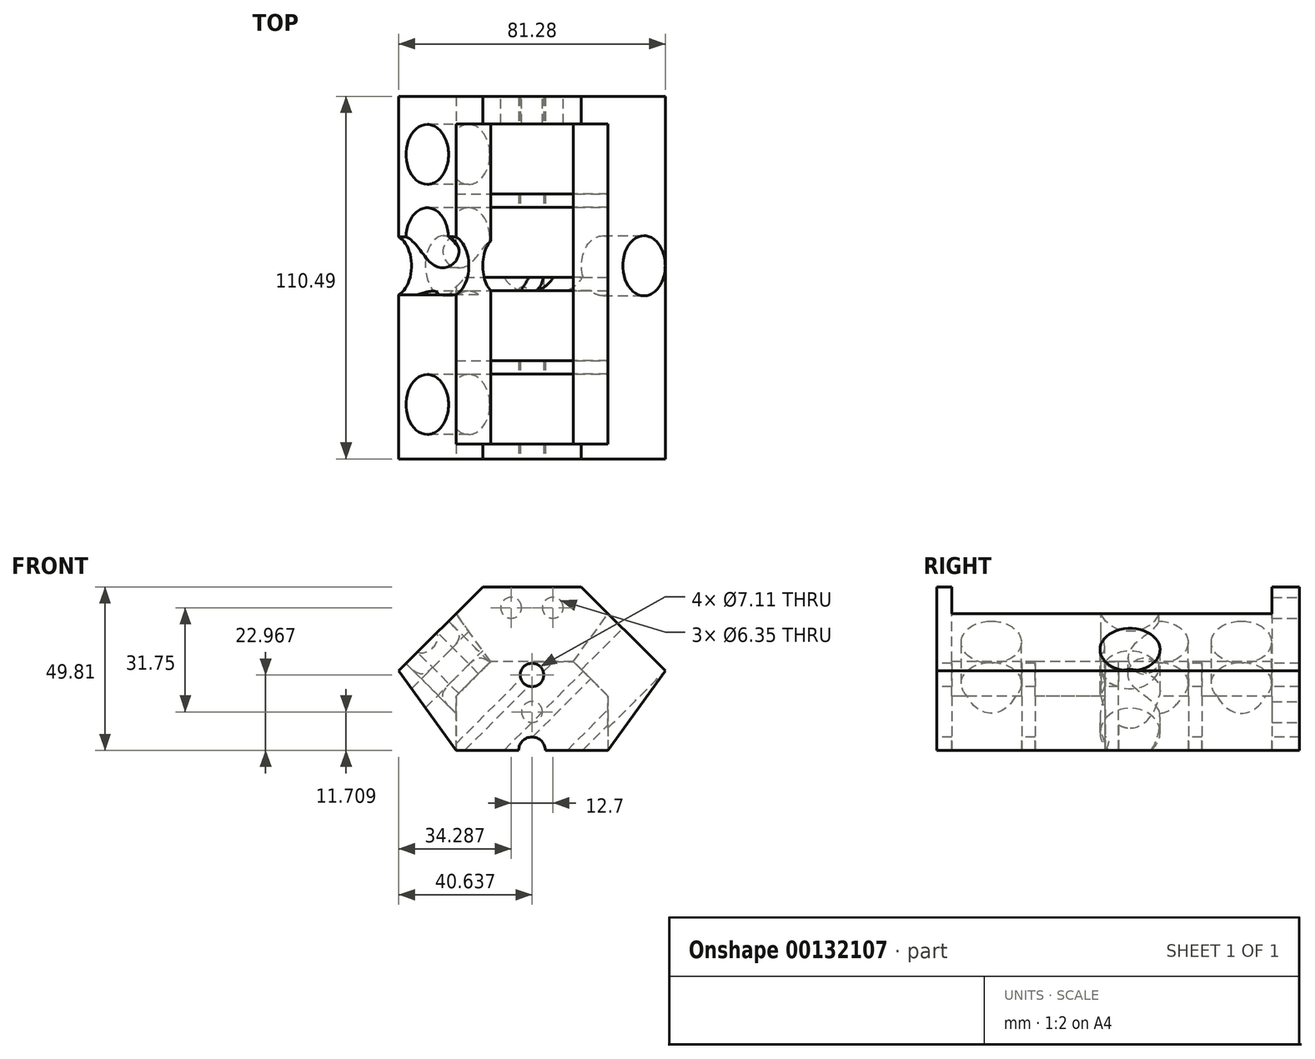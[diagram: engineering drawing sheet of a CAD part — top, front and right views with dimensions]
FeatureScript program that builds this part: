
annotation { "Feature Type Name" : "Feature", "Feature Type Description" : "" }
export const myFeature = defineFeature(function(context is Context, id is Id, definition is map)
    precondition{}
    {
        {
            var Q0;
            Q0=qCreatedBy(makeId("Top.planeOp"),FACE);
            var sketch = newSketch(context, id + "F0", { "sketchPlane" : qUnion([Q0])});
            skLineSegment(sketch, "E0.bottom", {"start": v(-50.32, 362.69) * mm, "end": v(356.08, 362.69) * mm});
            skLineSegment(sketch, "E0.top", {"start": v(-50.32, -189.76) * mm, "end": v(356.08, -189.76) * mm});
            skLineSegment(sketch, "E0.left", {"start": v(-50.32, 362.69) * mm, "end": v(-50.32, -189.76) * mm});
            skLineSegment(sketch, "E0.right", {"start": v(356.08, 362.69) * mm, "end": v(356.08, -189.76) * mm});
            skPoint(sketch, "E1.right.end.orphan", {"position": v(268.7, 221.15) * mm});
            skPoint(sketch, "E2.end.orphan", {"position": v(268.7, 119.55) * mm});
            skPoint(sketch, "E3.right.end.orphan", {"position": v(268.7, 66.78) * mm});
            skPoint(sketch, "E4.end.orphan", {"position": v(268.7, -34.82) * mm});
            skPoint(sketch, "E5.top.end.orphan", {"position": v(268.7, -62.76) * mm});
            skLineSegment(sketch, "E6.bottom", {"start": v(37.06, -166.9) * mm, "end": v(268.7, -166.9) * mm});
            skLineSegment(sketch, "E6.top", {"start": v(37.06, -60.22) * mm, "end": v(268.7, -60.22) * mm});
            skLineSegment(sketch, "E6.left", {"start": v(37.06, -166.9) * mm, "end": v(37.06, -60.22) * mm});
            skLineSegment(sketch, "E6.right", {"start": v(268.7, -166.9) * mm, "end": v(268.7, -60.22) * mm});
            skPoint(sketch, "E7.endSnap0", {"position": v(152.88, -189.76) * mm});
            skLineSegment(sketch, "E8.bottom", {"start": v(37.06, 320.78) * mm, "end": v(268.7, 320.78) * mm});
            skLineSegment(sketch, "E8.top", {"start": v(37.06, 214.1) * mm, "end": v(268.7, 214.1) * mm});
            skLineSegment(sketch, "E8.left", {"start": v(37.06, 320.78) * mm, "end": v(37.06, 214.1) * mm});
            skLineSegment(sketch, "E8.right", {"start": v(268.7, 320.78) * mm, "end": v(268.7, 214.1) * mm});
            skLineSegment(sketch, "E9.bottom", {"start": v(37.06, 193.78) * mm, "end": v(268.7, 193.78) * mm});
            skLineSegment(sketch, "E9.top", {"start": v(37.06, 87.1) * mm, "end": v(268.7, 87.1) * mm});
            skLineSegment(sketch, "E9.left", {"start": v(37.06, 193.78) * mm, "end": v(37.06, 87.1) * mm});
            skLineSegment(sketch, "E9.right", {"start": v(268.7, 193.78) * mm, "end": v(268.7, 87.1) * mm});
            skLineSegment(sketch, "E10.right", {"start": v(268.7, -34.82) * mm, "end": v(268.7, -39.9) * mm});
            skLineSegment(sketch, "E11.bottom", {"start": v(37.06, 66.78) * mm, "end": v(268.7, 66.78) * mm});
            skLineSegment(sketch, "E11.top", {"start": v(37.06, -39.9) * mm, "end": v(268.7, -39.9) * mm});
            skLineSegment(sketch, "E11.left", {"start": v(37.06, 66.78) * mm, "end": v(37.06, -39.9) * mm});
            skLineSegment(sketch, "E11.right", {"start": v(268.7, 66.78) * mm, "end": v(268.7, -39.9) * mm});
            skPoint(sketch, "E7.end.orphan", {"position": v(268.7, -189.76) * mm});
            skPoint(sketch, "E12.start.orphan", {"position": v(268.7, 320.78) * mm});
            skSolve(sketch);
        }
        {
            var Q0;
            Q0=makeQuery(id+"F0.imprint","IMPRINT",FACE,{"disambiguationData":[TD([[makeQuery(id+"F0.imprint","IMPRINT",EDGE,{"derivedFrom":sQuery(id+"F0.wireOp",EDGE,"E0.bottom")}),-1.0]])]});
            extrude(context, id + "F1", {"entities" : qUnion([Q0]), "depth" : 249.05 * mm});
        }
        {
            var Q0;
            Q0=makeQuery(id+"F1.opExtrude","SWEPT_FACE",FACE,{"disambiguationData":[OSD([sQuery(id+"F0.wireOp",EDGE,"E0.top")])]});
            var sketch = newSketch(context, id + "F2", { "sketchPlane" : qUnion([Q0])});
            skLineSegment(sketch, "E13", {"start": v(152.88, 0) * mm, "end": v(37.06, 0) * mm, "construction": true});
            skLineSegment(sketch, "E14", {"start": v(152.88, 0) * mm, "end": v(268.7, 0) * mm, "construction": true});
            skLineSegment(sketch, "E15", {"start": v(152.88, 0) * mm, "end": v(152.88, -265.94) * mm, "construction": true});
            skLineSegment(sketch, "E16", {"start": v(152.88, 0) * mm, "end": v(-102.56, -255.45) * mm, "construction": true});
            skLineSegment(sketch, "E17", {"start": v(-22.58, -175.46) * mm, "end": v(-184.67, -13.37) * mm, "construction": true});
            skLineSegment(sketch, "E18", {"start": v(-184.67, -13.37) * mm, "end": v(-50.32, 120.99) * mm, "construction": true});
            skLineSegment(sketch, "E19", {"start": v(37.06, 0) * mm, "end": v(-50.32, 120.99) * mm});
            skLineSegment(sketch, "E20", {"start": v(-50.32, 0) * mm, "end": v(37.06, 0) * mm});
            skLineSegment(sketch, "E21", {"start": v(-50.32, 120.99) * mm, "end": v(-50.32, 0) * mm});
            skLineSegment(sketch, "E22", {"start": v(152.88, 0) * mm, "end": v(426.24, -273.36) * mm, "construction": true});
            skLineSegment(sketch, "E23", {"start": v(328.35, -175.46) * mm, "end": v(490.44, -13.37) * mm, "construction": true});
            skLineSegment(sketch, "E24", {"start": v(490.44, -13.37) * mm, "end": v(356.08, 120.99) * mm, "construction": true});
            skLineSegment(sketch, "E25", {"start": v(268.7, 0) * mm, "end": v(356.08, 120.99) * mm});
            skLineSegment(sketch, "E26", {"start": v(356.08, 120.99) * mm, "end": v(356.08, 0) * mm});
            skLineSegment(sketch, "E27", {"start": v(268.7, 0) * mm, "end": v(356.08, 0) * mm});
            skLineSegment(sketch, "E28", {"start": v(-184.67, -13.37) * mm, "end": v(77.74, 249.05) * mm, "construction": true});
            skLineSegment(sketch, "E29", {"start": v(490.44, -13.37) * mm, "end": v(228.02, 249.05) * mm, "construction": true});
            skLineSegment(sketch, "E30", {"start": v(77.74, 249.05) * mm, "end": v(-50.32, 249.05) * mm});
            skLineSegment(sketch, "E31", {"start": v(-50.32, 249.05) * mm, "end": v(-50.32, 120.99) * mm});
            skLineSegment(sketch, "E32", {"start": v(-50.32, 120.99) * mm, "end": v(77.74, 249.05) * mm});
            skLineSegment(sketch, "E33", {"start": v(228.02, 249.05) * mm, "end": v(356.08, 249.05) * mm});
            skLineSegment(sketch, "E34", {"start": v(356.08, 249.05) * mm, "end": v(356.08, 120.99) * mm});
            skLineSegment(sketch, "E35", {"start": v(356.08, 120.99) * mm, "end": v(228.02, 249.05) * mm});
            skLineSegment(sketch, "E36", {"start": v(152.88, 249.05) * mm, "end": v(152.88, 344.64) * mm, "construction": true});
            skLineSegment(sketch, "E37", {"start": v(152.88, 344.64) * mm, "end": v(46.2, 344.64) * mm, "construction": true});
            skLineSegment(sketch, "E38", {"start": v(152.88, 344.64) * mm, "end": v(259.56, 344.64) * mm, "construction": true});
            skLineSegment(sketch, "E39", {"start": v(259.56, 344.64) * mm, "end": v(259.56, 217.5) * mm, "construction": true});
            skLineSegment(sketch, "E40", {"start": v(46.2, 344.64) * mm, "end": v(46.2, 217.5) * mm, "construction": true});
            skCircle(sketch, "E41", {"center": v(152.88, 0) * mm, "radius": 20.32 * mm});
            skLineSegment(sketch, "E42", {"start": v(152.88, 0) * mm, "end": v(152.88, 114.83) * mm, "construction": true});
            skCircle(sketch, "E43", {"center": v(152.88, 114.83) * mm, "radius": 17.78 * mm});
            skLineSegment(sketch, "E44", {"start": v(152.88, 114.83) * mm, "end": v(152.88, 132.61) * mm, "construction": true});
            skLineSegment(sketch, "E45", {"start": v(152.88, 132.61) * mm, "end": v(152.88, 249.05) * mm, "construction": true});
            skLineSegment(sketch, "E46", {"start": v(152.88, 249.05) * mm, "end": v(152.88, 147.45) * mm});
            skSolve(sketch);
        }
        {
            var Q0;
            Q0=makeQuery(id+"F2.imprint","IMPRINT",FACE,{"disambiguationData":[TD([[makeQuery(id+"F2.imprint","IMPRINT",EDGE,{"derivedFrom":sQuery(id+"F2.wireOp",EDGE,"E19")}),1.0]])]});
            extrude(context, id + "F3", {"entities" : qUnion([Q0]), "operationType" : NewBodyOperationType.REMOVE, "oppositeDirection" : true, "depth" : 1497.04 * mm});
        }
        {
            var Q0;
            Q0=makeQuery(id+"F2.imprint","IMPRINT",FACE,{"disambiguationData":[TD([[makeQuery(id+"F2.imprint","IMPRINT",EDGE,{"derivedFrom":sQuery(id+"F2.wireOp",EDGE,"E25")}),-1.0]])]});
            extrude(context, id + "F4", {"entities" : qUnion([Q0]), "operationType" : NewBodyOperationType.REMOVE, "oppositeDirection" : true, "depth" : 679.38 * mm});
        }
        {
            var Q0;
            Q0=makeQuery(id+"F2.imprint","IMPRINT",FACE,{"disambiguationData":[TD([[makeQuery(id+"F2.imprint","IMPRINT",EDGE,{"derivedFrom":sQuery(id+"F2.wireOp",EDGE,"E30")}),-1.0]])]});
            extrude(context, id + "F5", {"entities" : qUnion([Q0]), "operationType" : NewBodyOperationType.REMOVE, "oppositeDirection" : true, "depth" : 711.26 * mm});
        }
        {
            var Q0;
            Q0=makeQuery(id+"F2.imprint","IMPRINT",FACE,{"disambiguationData":[TD([[makeQuery(id+"F2.imprint","IMPRINT",EDGE,{"derivedFrom":sQuery(id+"F2.wireOp",EDGE,"E33")}),-1.0]])]});
            extrude(context, id + "F6", {"entities" : qUnion([Q0]), "operationType" : NewBodyOperationType.REMOVE, "oppositeDirection" : true, "depth" : 1229.88 * mm});
        }
        {
            var Q0;
            {var subQ0=sQuery(id+"F2.wireOp",EDGE,"E41");var subQ1=makeQuery(id+"F1.opExtrude","CAP_EDGE",EDGE,{"disambiguationData":[OSD([sQuery(id+"F0.wireOp",EDGE,"E0.top")])],"isStart":true});var subQ2=makeQuery(id+"F2.imprint","INTERSECT",VERTEX,{"disambiguationData":[OD(0.0)],"derivedFrom":[subQ1,subQ0]});Q0=makeQuery(id+"F2.imprint","IMPRINT",FACE,{"disambiguationData":[TD([[makeQuery(id+"F2.imprint","IMPRINT",EDGE,{"disambiguationData":[TD([[subQ2,1.0]])],"derivedFrom":subQ0}),1.0]])]});}
            extrude(context, id + "F7", {"entities" : qUnion([Q0]), "operationType" : NewBodyOperationType.REMOVE, "oppositeDirection" : true, "depth" : 578.05 * mm});
        }
        {
            var Q0;
            Q0=makeQuery(id+"F2.imprint","IMPRINT",FACE,{"disambiguationData":[TD([[makeQuery(id+"F2.imprint","IMPRINT",EDGE,{"derivedFrom":sQuery(id+"F2.wireOp",EDGE,"E43")}),1.0]])]});
            extrude(context, id + "F8", {"entities" : qUnion([Q0]), "operationType" : NewBodyOperationType.REMOVE, "oppositeDirection" : true, "depth" : 729.74 * mm});
        }
        {
            var Q0;
            Q0=makeQuery(id+"F1.opExtrude","SWEPT_FACE",FACE,{"disambiguationData":[OSD([sQuery(id+"F0.wireOp",EDGE,"E6.top")])]});
            var sketch = newSketch(context, id + "F9", { "sketchPlane" : qUnion([Q0])});
            skPoint(sketch, "E47.endSnap0", {"position": v(152.88, 249.05) * mm});
            skLineSegment(sketch, "E48", {"start": v(152.88, 135.38) * mm, "end": v(37.06, 135.38) * mm});
            skLineSegment(sketch, "E49", {"start": v(37.06, 135.38) * mm, "end": v(268.7, 135.38) * mm});
            skLineSegment(sketch, "E50", {"start": v(268.7, 135.38) * mm, "end": v(268.7, 208.36) * mm});
            skLineSegment(sketch, "E51", {"start": v(268.7, 208.36) * mm, "end": v(228.02, 249.05) * mm});
            skLineSegment(sketch, "E52", {"start": v(228.02, 249.05) * mm, "end": v(77.74, 249.05) * mm});
            skLineSegment(sketch, "E53", {"start": v(77.74, 249.05) * mm, "end": v(37.06, 208.36) * mm});
            skLineSegment(sketch, "E54", {"start": v(37.06, 135.38) * mm, "end": v(37.06, 208.36) * mm});
            skLineSegment(sketch, "E55", {"start": v(37.06, 208.36) * mm, "end": v(89.77, 135.38) * mm});
            skLineSegment(sketch, "E56", {"start": v(268.7, 208.36) * mm, "end": v(216, 135.38) * mm});
            skSolve(sketch);
        }
        {
            var Q0;
            Q0=makeQuery(id+"F9.imprint","IMPRINT",FACE,{"disambiguationData":[TD([[makeQuery(id+"F9.imprint","IMPRINT",EDGE,{"derivedFrom":sQuery(id+"F9.wireOp",EDGE,"E51")}),-1.0]])]});
            extrude(context, id + "F10", {"entities" : qUnion([Q0]), "operationType" : NewBodyOperationType.REMOVE, "oppositeDirection" : true, "depth" : 324.26 * mm});
        }
        {
            var Q0;
            Q0=makeQuery(id+"F1.opExtrude","SWEPT_FACE",FACE,{"disambiguationData":[OSD([sQuery(id+"F0.wireOp",EDGE,"E11.top")])]});
            var sketch = newSketch(context, id + "F11", { "sketchPlane" : qUnion([Q0])});
            skLineSegment(sketch, "E57", {"start": v(-89.77, 135.38) * mm, "end": v(-37.06, 208.36) * mm});
            skLineSegment(sketch, "E58", {"start": v(-89.77, 135.38) * mm, "end": v(-37.06, 135.38) * mm});
            skLineSegment(sketch, "E59", {"start": v(-37.06, 135.38) * mm, "end": v(-37.06, 208.36) * mm});
            skSolve(sketch);
        }
        {
            var Q0;
            Q0=qSketchRegion(id+"F11",true);
            extrude(context, id + "F12", {"entities" : qUnion([Q0]), "operationType" : NewBodyOperationType.ADD, "depth" : 368.3 * mm, "hasSecondDirection" : true, "secondDirectionOppositeDirection" : true, "secondDirectionDepth" : 127 * mm});
        }
        {
            var Q0;
            Q0=makeQuery(id+"F1.opExtrude","SWEPT_FACE",FACE,{"disambiguationData":[OSD([sQuery(id+"F0.wireOp",EDGE,"E11.top")])]});
            var sketch = newSketch(context, id + "F13", { "sketchPlane" : qUnion([Q0])});
            skLineSegment(sketch, "E60", {"start": v(-216, 135.38) * mm, "end": v(-268.7, 135.38) * mm});
            skLineSegment(sketch, "E61", {"start": v(-268.7, 135.38) * mm, "end": v(-268.7, 208.36) * mm});
            skLineSegment(sketch, "E62", {"start": v(-268.7, 208.36) * mm, "end": v(-216, 135.38) * mm});
            skSolve(sketch);
        }
        {
            var Q0;
            Q0=qSketchRegion(id+"F13",true);
            extrude(context, id + "F14", {"entities" : qUnion([Q0]), "operationType" : NewBodyOperationType.ADD, "depth" : 368.3 * mm, "hasSecondDirection" : true, "secondDirectionOppositeDirection" : true, "secondDirectionDepth" : 127 * mm});
        }
        {
            var Q0;
            Q0=makeQuery(id+"F1.opExtrude","SWEPT_FACE",FACE,{"disambiguationData":[OSD([sQuery(id+"F0.wireOp",EDGE,"E9.top")])]});
            var sketch = newSketch(context, id + "F15", { "sketchPlane" : qUnion([Q0])});
            skLineSegment(sketch, "E63", {"start": v(-89.77, 135.38) * mm, "end": v(-37.06, 82.68) * mm});
            skLineSegment(sketch, "E64", {"start": v(-37.06, 82.68) * mm, "end": v(-37.06, 135.38) * mm});
            skLineSegment(sketch, "E65", {"start": v(-37.06, 135.38) * mm, "end": v(-89.77, 135.38) * mm});
            skLineSegment(sketch, "E66", {"start": v(-216, 135.38) * mm, "end": v(-268.7, 82.68) * mm});
            skLineSegment(sketch, "E67", {"start": v(-268.7, 82.68) * mm, "end": v(-268.7, 135.38) * mm});
            skLineSegment(sketch, "E68", {"start": v(-268.7, 135.38) * mm, "end": v(-216, 135.38) * mm});
            skSolve(sketch);
        }
        {
            var Q0;
            Q0=makeQuery(id+"F15.imprint","IMPRINT",FACE,{"disambiguationData":[TD([[makeQuery(id+"F15.imprint","IMPRINT",EDGE,{"derivedFrom":sQuery(id+"F15.wireOp",EDGE,"E63")}),1.0]])]});
            extrude(context, id + "F16", {"entities" : qUnion([Q0]), "operationType" : NewBodyOperationType.ADD, "depth" : 249.12 * mm, "hasSecondDirection" : true, "secondDirectionOppositeDirection" : true, "secondDirectionDepth" : 267.4 * mm});
        }
        {
            var Q0;
            Q0=makeQuery(id+"F15.imprint","IMPRINT",FACE,{"disambiguationData":[TD([[makeQuery(id+"F15.imprint","IMPRINT",EDGE,{"derivedFrom":sQuery(id+"F15.wireOp",EDGE,"E66")}),-1.0]])]});
            extrude(context, id + "F17", {"entities" : qUnion([Q0]), "operationType" : NewBodyOperationType.ADD, "depth" : 272.47 * mm, "hasSecondDirection" : true, "secondDirectionOppositeDirection" : true, "secondDirectionDepth" : 265.33 * mm});
        }
        {
            var Q0;
            Q0=makeQuery(id+"F6.boolean.opBoolean","COPY",FACE,{"derivedFrom":makeQuery(id+"F6.opExtrude","SWEPT_FACE",FACE,{"disambiguationData":[OSD([sQuery(id+"F2.wireOp",EDGE,"E35")])]})});
            var sketch = newSketch(context, id + "F18", { "sketchPlane" : qUnion([Q0])});
            skLineSegment(sketch, "E69", {"start": v(42.67, -166.9) * mm, "end": v(166.24, -166.9) * mm});
            skLineSegment(sketch, "E70", {"start": v(42.67, 320.78) * mm, "end": v(166.24, 320.78) * mm});
            skLineSegment(sketch, "E71", {"start": v(104.45, -166.9) * mm, "end": v(104.45, -60.22) * mm});
            skLineSegment(sketch, "E72", {"start": v(104.45, -39.9) * mm, "end": v(104.45, 66.78) * mm});
            skLineSegment(sketch, "E73", {"start": v(104.45, 87.1) * mm, "end": v(104.45, 193.78) * mm});
            skLineSegment(sketch, "E74", {"start": v(104.45, 214.1) * mm, "end": v(104.45, 320.78) * mm});
            skLineSegment(sketch, "E75", {"start": v(104.45, -113.56) * mm, "end": v(166.24, -113.56) * mm});
            skLineSegment(sketch, "E76", {"start": v(104.45, 13.44) * mm, "end": v(166.24, 13.44) * mm});
            skLineSegment(sketch, "E77", {"start": v(104.45, 140.44) * mm, "end": v(166.24, 140.44) * mm});
            skLineSegment(sketch, "E78", {"start": v(104.45, 267.44) * mm, "end": v(166.24, 267.44) * mm});
            skLineSegment(sketch, "E79", {"start": v(119.9, -120.23) * mm, "end": v(104.45, -120.23) * mm});
            skCircle(sketch, "E80", {"center": v(104.45, -120.23) * mm, "radius": 45.72 * mm});
            skLineSegment(sketch, "E81", {"start": v(135.35, 13.44) * mm, "end": v(135.35, 6.75) * mm});
            skLineSegment(sketch, "E82", {"start": v(135.35, 140.44) * mm, "end": v(135.35, 133.75) * mm});
            skLineSegment(sketch, "E83", {"start": v(135.35, 267.44) * mm, "end": v(135.35, 260.75) * mm});
            skLineSegment(sketch, "E84", {"start": v(135.35, 6.75) * mm, "end": v(104.45, 6.75) * mm});
            skLineSegment(sketch, "E85", {"start": v(135.35, 133.75) * mm, "end": v(104.45, 133.75) * mm});
            skLineSegment(sketch, "E86", {"start": v(135.35, 260.75) * mm, "end": v(104.45, 260.75) * mm});
            skCircle(sketch, "E87", {"center": v(104.45, 6.75) * mm, "radius": 45.72 * mm});
            skCircle(sketch, "E88", {"center": v(104.45, 133.75) * mm, "radius": 45.72 * mm});
            skCircle(sketch, "E89", {"center": v(104.45, 260.75) * mm, "radius": 45.72 * mm});
            skSolve(sketch);
        }
        {
            var Q0;
            Q0 = qSketchRegion(id + "F18", true);
            var Q1;
            {var subQ4=sQuery(id+"F18.wireOp",EDGE,"E81");Q1=makeQuery(id+"F18.imprint","IMPRINT",FACE,{"disambiguationData":[TD([[makeQuery(id+"F18.imprint","IMPRINT",EDGE,{"derivedFrom":subQ4}),-1.0]])]});}
            var Q2;
            {var subQ4=sQuery(id+"F18.wireOp",EDGE,"E82");Q2=makeQuery(id+"F18.imprint","IMPRINT",FACE,{"disambiguationData":[TD([[makeQuery(id+"F18.imprint","IMPRINT",EDGE,{"derivedFrom":subQ4}),-1.0]])]});}
            var Q3;
            {var subQ4=sQuery(id+"F18.wireOp",EDGE,"E83");Q3=makeQuery(id+"F18.imprint","IMPRINT",FACE,{"disambiguationData":[TD([[makeQuery(id+"F18.imprint","IMPRINT",EDGE,{"derivedFrom":subQ4}),-1.0]])]});}
            extrude(context, id + "F19", {"entities" : qUnion([Q0, Q1, Q2, Q3]), "operationType" : NewBodyOperationType.REMOVE, "oppositeDirection" : true, "depth" : 558.8 * mm});
        }
        {
            var Q0;
            Q0=makeQuery(id+"F5.boolean.opBoolean","COPY",FACE,{"derivedFrom":makeQuery(id+"F5.opExtrude","SWEPT_FACE",FACE,{"disambiguationData":[OSD([sQuery(id+"F2.wireOp",EDGE,"E32")])]})});
            var sketch = newSketch(context, id + "F20", { "sketchPlane" : qUnion([Q0])});
            skLineSegment(sketch, "E90", {"start": v(-320.78, 173.54) * mm, "end": v(-320.78, 49.97) * mm});
            skLineSegment(sketch, "E91", {"start": v(-320.78, 111.76) * mm, "end": v(-319.84, 111.76) * mm});
            skLineSegment(sketch, "E92", {"start": v(-193.78, 111.76) * mm, "end": v(-192.84, 111.76) * mm});
            skLineSegment(sketch, "E93", {"start": v(-66.78, 111.76) * mm, "end": v(-65.84, 111.76) * mm});
            skLineSegment(sketch, "E94", {"start": v(60.22, 111.76) * mm, "end": v(61.16, 111.76) * mm});
            skCircle(sketch, "E95", {"center": v(-274.12, 111.76) * mm, "radius": 45.72 * mm});
            skCircle(sketch, "E96", {"center": v(-147.12, 111.76) * mm, "radius": 45.72 * mm});
            skCircle(sketch, "E97", {"center": v(-20.12, 111.76) * mm, "radius": 45.72 * mm});
            skCircle(sketch, "E98", {"center": v(106.88, 111.76) * mm, "radius": 45.72 * mm});
            skPoint(sketch, "E99.start.orphan", {"position": v(-267.44, 111.76) * mm});
            skLineSegment(sketch, "E100.trimOffspring", {"start": v(-228.4, 111.76) * mm, "end": v(-214.1, 111.76) * mm});
            skLineSegment(sketch, "E101.trimOffspring", {"start": v(-101.4, 111.76) * mm, "end": v(-87.1, 111.76) * mm});
            skPoint(sketch, "E102.orphan", {"position": v(-140.44, 111.76) * mm});
            skPoint(sketch, "E103.start.orphan", {"position": v(-13.44, 111.76) * mm});
            skLineSegment(sketch, "E104.trimOffspring", {"start": v(25.6, 111.76) * mm, "end": v(39.9, 111.76) * mm});
            skPoint(sketch, "E105.start.orphan", {"position": v(113.56, 111.76) * mm});
            skLineSegment(sketch, "E106.trimOffspring", {"start": v(152.6, 111.76) * mm, "end": v(166.9, 111.76) * mm});
            skSolve(sketch);
        }
        {
            var Q0;
            {var subQ0=sQuery(id+"F20.wireOp",EDGE,"E95");var subQ1=makeQuery(id+"F20.imprint","IMPRINT",VERTEX,{"disambiguationData":[OD(0.0)],"derivedFrom":subQ0});Q0=makeQuery(id+"F20.imprint","IMPRINT",FACE,{"disambiguationData":[TD([[makeQuery(id+"F20.imprint","IMPRINT",EDGE,{"disambiguationData":[TD([[subQ1,1.0]])],"derivedFrom":subQ0}),1.0]])]});}
            var Q1;
            {var subQ0=sQuery(id+"F20.wireOp",EDGE,"E96");var subQ1=makeQuery(id+"F20.imprint","IMPRINT",VERTEX,{"disambiguationData":[OD(0.0)],"derivedFrom":subQ0});Q1=makeQuery(id+"F20.imprint","IMPRINT",FACE,{"disambiguationData":[TD([[makeQuery(id+"F20.imprint","IMPRINT",EDGE,{"disambiguationData":[TD([[subQ1,1.0]])],"derivedFrom":subQ0}),1.0]])]});}
            var Q2;
            {var subQ0=sQuery(id+"F20.wireOp",EDGE,"E97");var subQ1=makeQuery(id+"F20.imprint","IMPRINT",VERTEX,{"disambiguationData":[OD(0.0)],"derivedFrom":subQ0});Q2=makeQuery(id+"F20.imprint","IMPRINT",FACE,{"disambiguationData":[TD([[makeQuery(id+"F20.imprint","IMPRINT",EDGE,{"disambiguationData":[TD([[subQ1,1.0]])],"derivedFrom":subQ0}),1.0]])]});}
            var Q3;
            {var subQ0=sQuery(id+"F20.wireOp",EDGE,"E98");var subQ1=makeQuery(id+"F20.imprint","IMPRINT",VERTEX,{"disambiguationData":[OD(0.0)],"derivedFrom":subQ0});Q3=makeQuery(id+"F20.imprint","IMPRINT",FACE,{"disambiguationData":[TD([[makeQuery(id+"F20.imprint","IMPRINT",EDGE,{"disambiguationData":[TD([[subQ1,1.0]])],"derivedFrom":subQ0}),1.0]])]});}
            extrude(context, id + "F21", {"entities" : qUnion([Q0, Q1, Q2, Q3]), "operationType" : NewBodyOperationType.REMOVE, "oppositeDirection" : true, "depth" : 558.8 * mm});
        }
        {
            var Q0;
            Q0=makeQuery(id+"F1.opExtrude","SWEPT_BODY",BODY,{"disambiguationData":[OSD([sQuery(id+"F0.wireOp",EDGE,"E0.bottom"),sQuery(id+"F0.wireOp",EDGE,"E0.top"),sQuery(id+"F0.wireOp",EDGE,"E0.left"),sQuery(id+"F0.wireOp",EDGE,"E0.right"),sQuery(id+"F0.wireOp",EDGE,"E6.bottom"),sQuery(id+"F0.wireOp",EDGE,"E6.top"),sQuery(id+"F0.wireOp",EDGE,"E6.left"),sQuery(id+"F0.wireOp",EDGE,"E6.right"),sQuery(id+"F0.wireOp",EDGE,"E8.bottom"),sQuery(id+"F0.wireOp",EDGE,"E8.top"),sQuery(id+"F0.wireOp",EDGE,"E8.left"),sQuery(id+"F0.wireOp",EDGE,"E8.right"),sQuery(id+"F0.wireOp",EDGE,"E9.bottom"),sQuery(id+"F0.wireOp",EDGE,"E9.top"),sQuery(id+"F0.wireOp",EDGE,"E9.left"),sQuery(id+"F0.wireOp",EDGE,"E9.right"),sQuery(id+"F0.wireOp",EDGE,"E11.bottom"),sQuery(id+"F0.wireOp",EDGE,"E11.top"),sQuery(id+"F0.wireOp",EDGE,"E11.left"),sQuery(id+"F0.wireOp",EDGE,"E11.right")])]});
            var Q1;
            Q1=qCreatedBy(makeId("Origin.pointOp"),VERTEX);
            transform(context, id + "F22", {"entities" : qUnion([Q0]), "transformType" : TransformType.SCALE_UNIFORMLY, "scale" : .2, "scalePoint" : qUnion([Q1]), "makeCopy" : false});
        }
        {
            var Q0;
            Q0=makeQuery(id+"F1.opExtrude","SWEPT_FACE",FACE,{"disambiguationData":[OSD([sQuery(id+"F0.wireOp",EDGE,"E0.bottom")])]});
            var sketch = newSketch(context, id + "F23", { "sketchPlane" : qUnion([Q0])});
            skLineSegment(sketch, "E107", {"start": v(-30.58, 49.8) * mm, "end": v(-30.58, 37.1) * mm});
            skLineSegment(sketch, "E108", {"start": v(-30.58, 37.1) * mm, "end": v(-17.88, 37.1) * mm});
            skLineSegment(sketch, "E109", {"start": v(-30.58, 37.1) * mm, "end": v(-43.28, 37.1) * mm});
            skLineSegment(sketch, "E110", {"start": v(-43.28, 37.1) * mm, "end": v(-43.28, 49.8) * mm});
            skLineSegment(sketch, "E111", {"start": v(-17.88, 37.1) * mm, "end": v(-17.88, 49.8) * mm});
            skLineSegment(sketch, "E112", {"start": v(-43.28, 43.46) * mm, "end": v(-36.93, 43.46) * mm});
            skLineSegment(sketch, "E113", {"start": v(-17.88, 43.46) * mm, "end": v(-24.23, 43.46) * mm});
            skCircle(sketch, "E114", {"center": v(-36.93, 43.46) * mm, "radius": 3.18 * mm});
            skCircle(sketch, "E115", {"center": v(-24.23, 43.46) * mm, "radius": 3.18 * mm});
            skSolve(sketch);
        }
        {
            var Q0;
            Q0 = qSketchRegion(id + "F23", true);
            extrude(context, id + "F24", {"entities" : qUnion([Q0]), "operationType" : NewBodyOperationType.REMOVE, "oppositeDirection" : true, "depth" : 25.4 * mm});
        }
        {
            var Q0;
            Q0=makeQuery(id+"F1.opExtrude","SWEPT_FACE",FACE,{"disambiguationData":[OSD([sQuery(id+"F0.wireOp",EDGE,"E0.bottom")])]});
            var sketch = newSketch(context, id + "F25", { "sketchPlane" : qUnion([Q0])});
            skLineSegment(sketch, "E116", {"start": v(-30.58, 49.8) * mm, "end": v(-30.58, 11.7) * mm});
            skCircle(sketch, "E117", {"center": v(-30.58, 11.7) * mm, "radius": 3.18 * mm});
            skSolve(sketch);
        }
        {
            var Q0;
            Q0 = qSketchRegion(id + "F25", true);
            extrude(context, id + "F26", {"entities" : qUnion([Q0]), "operationType" : NewBodyOperationType.REMOVE, "oppositeDirection" : true, "depth" : 25.4 * mm});
        }
    });
